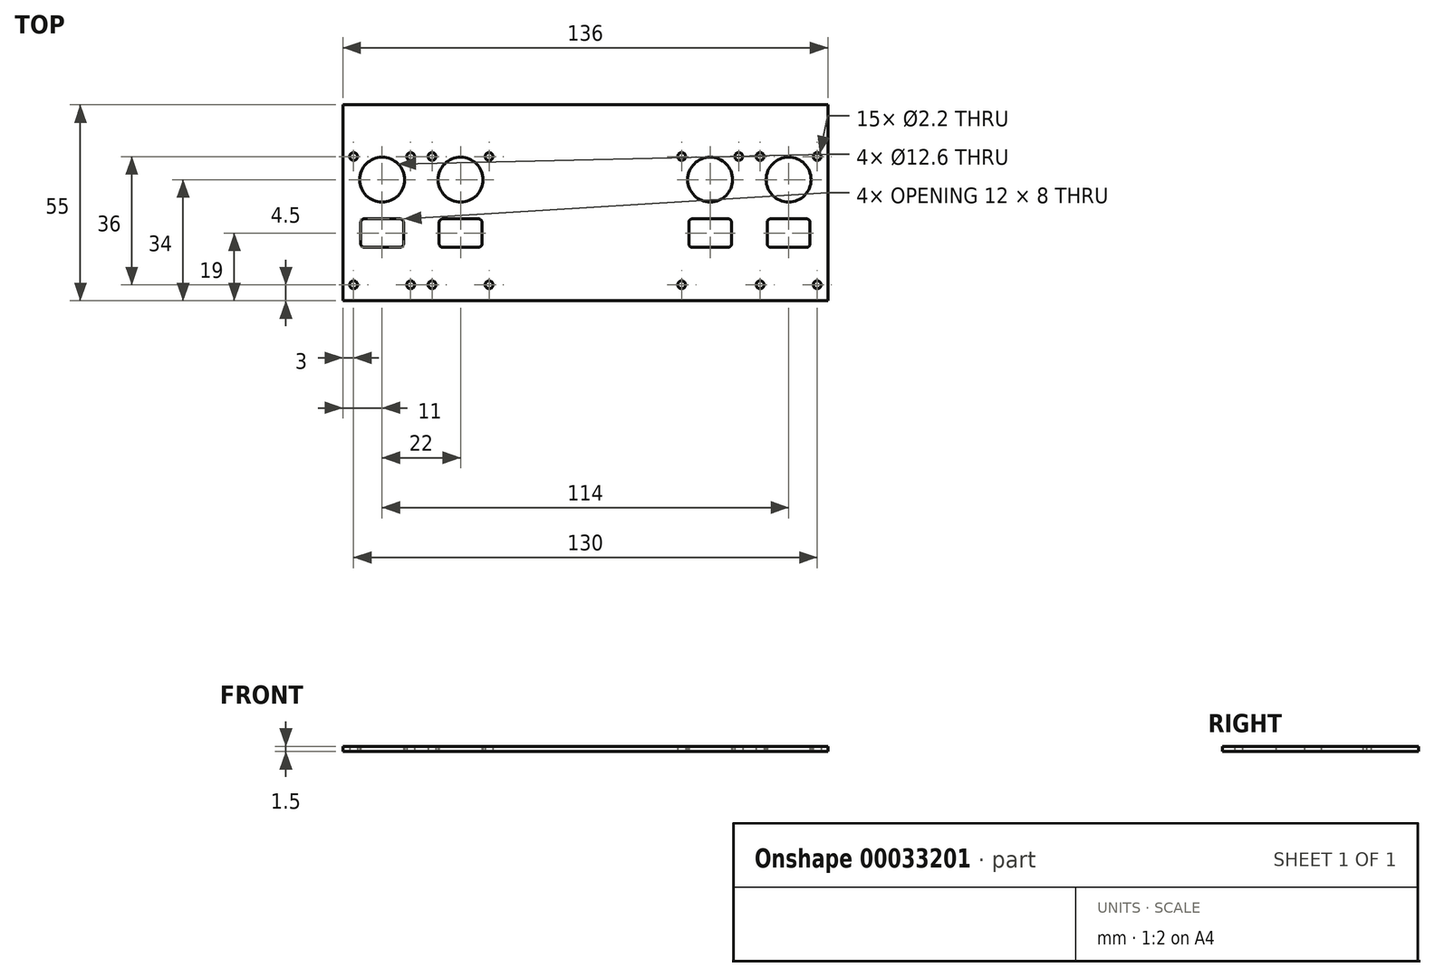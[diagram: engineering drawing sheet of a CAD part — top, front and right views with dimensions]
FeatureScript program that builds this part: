
annotation { "Feature Type Name" : "Feature", "Feature Type Description" : "" }
export const myFeature = defineFeature(function(context is Context, id is Id, definition is map)
    precondition{}
    {
        {
            var Q0;
            Q0=qCreatedBy(makeId("Top.planeOp"),FACE);
            var sketch = newSketch(context, id + "F0", { "sketchPlane" : qUnion([Q0])});
            skLineSegment(sketch, "E0.bottom", {"start": v(-68, 27.5) * mm, "end": v(68, 27.5) * mm});
            skLineSegment(sketch, "E0.top", {"start": v(-68, -27.5) * mm, "end": v(68, -27.5) * mm});
            skLineSegment(sketch, "E0.left", {"start": v(-68, 27.5) * mm, "end": v(-68, -27.5) * mm});
            skLineSegment(sketch, "E0.right", {"start": v(68, 27.5) * mm, "end": v(68, -27.5) * mm});
            skPoint(sketch, "E0.middle", {"position": v(0, 0) * mm});
            skLineSegment(sketch, "E1", {"start": v(-57, 27.5) * mm, "end": v(-57, -27.5) * mm, "construction": true});
            skCircle(sketch, "E2", {"center": v(-65, 13) * mm, "radius": 1.1 * mm});
            skCircle(sketch, "E3", {"center": v(-65, -23) * mm, "radius": 1.1 * mm});
            skCircle(sketch, "E4.MirrorC", {"center": v(-49, 13) * mm, "radius": 1.1 * mm});
            skCircle(sketch, "E5.MirrorC", {"center": v(-49, -23) * mm, "radius": 1.1 * mm});
            skCircle(sketch, "E6", {"center": v(-57, 6.5) * mm, "radius": 6.3 * mm});
            skCircle(sketch, "E7.MirrorC", {"center": v(49, -23) * mm, "radius": 1.1 * mm});
            skCircle(sketch, "E8.MirrorC", {"center": v(57, 6.5) * mm, "radius": 6.3 * mm});
            skCircle(sketch, "E9.MirrorC", {"center": v(49, 13) * mm, "radius": 1.1 * mm});
            skCircle(sketch, "E10.MirrorC", {"center": v(65, 13) * mm, "radius": 1.1 * mm});
            skCircle(sketch, "E11.MirrorC", {"center": v(65, -23) * mm, "radius": 1.1 * mm});
            skLineSegment(sketch, "E12.bottom", {"start": v(-52, -12.5) * mm, "end": v(-62, -12.5) * mm});
            skLineSegment(sketch, "E12.top", {"start": v(-52, -4.5) * mm, "end": v(-62, -4.5) * mm});
            skLineSegment(sketch, "E12.left", {"start": v(-51, -11.5) * mm, "end": v(-51, -5.5) * mm});
            skLineSegment(sketch, "E12.right", {"start": v(-63, -11.5) * mm, "end": v(-63, -5.5) * mm});
            skPoint(sketch, "E12.middle", {"position": v(-57, -8.5) * mm});
            skPoint(sketch, "E13.visualSharp", {"position": v(-63, -4.5) * mm});
            skArc(sketch, "E13.filletArc", {"start": v(-62, -4.5) * mm, "mid": v(-62.7, -4.8) * mm, "end": v(-63, -5.5) * mm});
            skPoint(sketch, "E14.visualSharp", {"position": v(-63, -12.5) * mm});
            skArc(sketch, "E14.filletArc", {"start": v(-63, -11.5) * mm, "mid": v(-62.7, -12.2) * mm, "end": v(-62, -12.5) * mm});
            skPoint(sketch, "E15.visualSharp", {"position": v(-51, -12.5) * mm});
            skArc(sketch, "E15.filletArc", {"start": v(-52, -12.5) * mm, "mid": v(-51.3, -12.2) * mm, "end": v(-51, -11.5) * mm});
            skPoint(sketch, "E16.visualSharp", {"position": v(-51, -4.5) * mm});
            skArc(sketch, "E16.filletArc", {"start": v(-51, -5.5) * mm, "mid": v(-51.3, -4.8) * mm, "end": v(-52, -4.5) * mm});
            skArc(sketch, "E17.MirrorCS", {"start": v(62, -4.5) * mm, "mid": v(62.7, -4.8) * mm, "end": v(63, -5.5) * mm});
            skArc(sketch, "E18.MirrorCS", {"start": v(52, -12.5) * mm, "mid": v(51.3, -12.2) * mm, "end": v(51, -11.5) * mm});
            skArc(sketch, "E19.MirrorCS", {"start": v(51, -5.5) * mm, "mid": v(51.3, -4.8) * mm, "end": v(52, -4.5) * mm});
            skArc(sketch, "E20.MirrorCS", {"start": v(63, -11.5) * mm, "mid": v(62.7, -12.2) * mm, "end": v(62, -12.5) * mm});
            skLineSegment(sketch, "E21.MirrorCS", {"start": v(63, -11.5) * mm, "end": v(63, -5.5) * mm});
            skLineSegment(sketch, "E22.MirrorCS", {"start": v(52, -12.5) * mm, "end": v(62, -12.5) * mm});
            skPoint(sketch, "E23.MirrorP", {"position": v(51, -12.5) * mm});
            skPoint(sketch, "E24.MirrorP", {"position": v(63, -12.5) * mm});
            skPoint(sketch, "E25.MirrorP", {"position": v(63, -4.5) * mm});
            skPoint(sketch, "E26.MirrorP", {"position": v(57, -8.5) * mm});
            skLineSegment(sketch, "E27.MirrorCS", {"start": v(52, -4.5) * mm, "end": v(62, -4.5) * mm});
            skLineSegment(sketch, "E28.MirrorCS", {"start": v(51, -11.5) * mm, "end": v(51, -5.5) * mm});
            skPoint(sketch, "E29.MirrorP", {"position": v(51, -4.5) * mm});
            skLineSegment(sketch, "E30", {"start": v(-46, 27.5) * mm, "end": v(-46, -27.5) * mm, "construction": true});
            skArc(sketch, "E31.MirrorCS", {"start": v(-41, -5.5) * mm, "mid": v(-40.7, -4.8) * mm, "end": v(-40, -4.5) * mm});
            skArc(sketch, "E32.MirrorCS", {"start": v(-29, -11.5) * mm, "mid": v(-29.3, -12.2) * mm, "end": v(-30, -12.5) * mm});
            skArc(sketch, "E33.MirrorCS", {"start": v(-40, -12.5) * mm, "mid": v(-40.7, -12.2) * mm, "end": v(-41, -11.5) * mm});
            skArc(sketch, "E34.MirrorCS", {"start": v(-30, -4.5) * mm, "mid": v(-29.3, -4.8) * mm, "end": v(-29, -5.5) * mm});
            skCircle(sketch, "E35.MirrorC", {"center": v(-27, -23) * mm, "radius": 1.1 * mm});
            skCircle(sketch, "E36.MirrorC", {"center": v(-43, 13) * mm, "radius": 1.1 * mm});
            skCircle(sketch, "E37.MirrorC", {"center": v(-43, -23) * mm, "radius": 1.1 * mm});
            skLineSegment(sketch, "E38.MirrorCS", {"start": v(-29, -11.5) * mm, "end": v(-29, -5.5) * mm});
            skCircle(sketch, "E39.MirrorC", {"center": v(-35, 6.5) * mm, "radius": 6.3 * mm});
            skLineSegment(sketch, "E40.MirrorCS", {"start": v(-40, -4.5) * mm, "end": v(-30, -4.5) * mm});
            skPoint(sketch, "E41.MirrorP", {"position": v(-35, -8.5) * mm});
            skLineSegment(sketch, "E42.MirrorCS", {"start": v(-41, -11.5) * mm, "end": v(-41, -5.5) * mm});
            skPoint(sketch, "E43.MirrorP", {"position": v(-29, -12.5) * mm});
            skPoint(sketch, "E44.MirrorP", {"position": v(-29, -4.5) * mm});
            skLineSegment(sketch, "E45.MirrorCS", {"start": v(-40, -12.5) * mm, "end": v(-30, -12.5) * mm});
            skPoint(sketch, "E46.MirrorP", {"position": v(-41, -12.5) * mm});
            skPoint(sketch, "E47.MirrorP", {"position": v(-41, -4.5) * mm});
            skCircle(sketch, "E48.MirrorC", {"center": v(-27, 13) * mm, "radius": 1.1 * mm});
            skArc(sketch, "E49.MirrorCS", {"start": v(29, -11.5) * mm, "mid": v(29.3, -12.2) * mm, "end": v(30, -12.5) * mm});
            skArc(sketch, "E50.MirrorCS", {"start": v(40, -12.5) * mm, "mid": v(40.7, -12.2) * mm, "end": v(41, -11.5) * mm});
            skArc(sketch, "E51.MirrorCS", {"start": v(30, -4.5) * mm, "mid": v(29.3, -4.8) * mm, "end": v(29, -5.5) * mm});
            skArc(sketch, "E52.MirrorCS", {"start": v(41, -5.5) * mm, "mid": v(40.7, -4.8) * mm, "end": v(40, -4.5) * mm});
            skLineSegment(sketch, "E53.MirrorCS", {"start": v(29, -11.5) * mm, "end": v(29, -5.5) * mm});
            skLineSegment(sketch, "E54.MirrorCS", {"start": v(40, -12.5) * mm, "end": v(30, -12.5) * mm});
            skLineSegment(sketch, "E55.MirrorCS", {"start": v(41, -11.5) * mm, "end": v(41, -5.5) * mm});
            skPoint(sketch, "E56.MirrorP", {"position": v(29, -12.5) * mm});
            skPoint(sketch, "E57.MirrorP", {"position": v(29, -4.5) * mm});
            skCircle(sketch, "E58.MirrorC", {"center": v(27, -23) * mm, "radius": 1.1 * mm});
            skPoint(sketch, "E59.MirrorP", {"position": v(41, -4.5) * mm});
            skCircle(sketch, "E60.MirrorC", {"center": v(27, 13) * mm, "radius": 1.1 * mm});
            skLineSegment(sketch, "E61.MirrorCS", {"start": v(40, -4.5) * mm, "end": v(30, -4.5) * mm});
            skPoint(sketch, "E62.MirrorP", {"position": v(41, -12.5) * mm});
            skPoint(sketch, "E63.MirrorP", {"position": v(35, -8.5) * mm});
            skCircle(sketch, "E64.MirrorC", {"center": v(35, 6.5) * mm, "radius": 6.3 * mm});
            skCircle(sketch, "E65.MirrorC", {"center": v(43, 13) * mm, "radius": 1.1 * mm});
            skSolve(sketch);
        }
        {
            var Q0;
            Q0=qSketchRegion(id+"F0",true);
            extrude(context, id + "F1", {"entities" : qUnion([Q0]), "depth" : 1.5 * mm});
        }
    });
